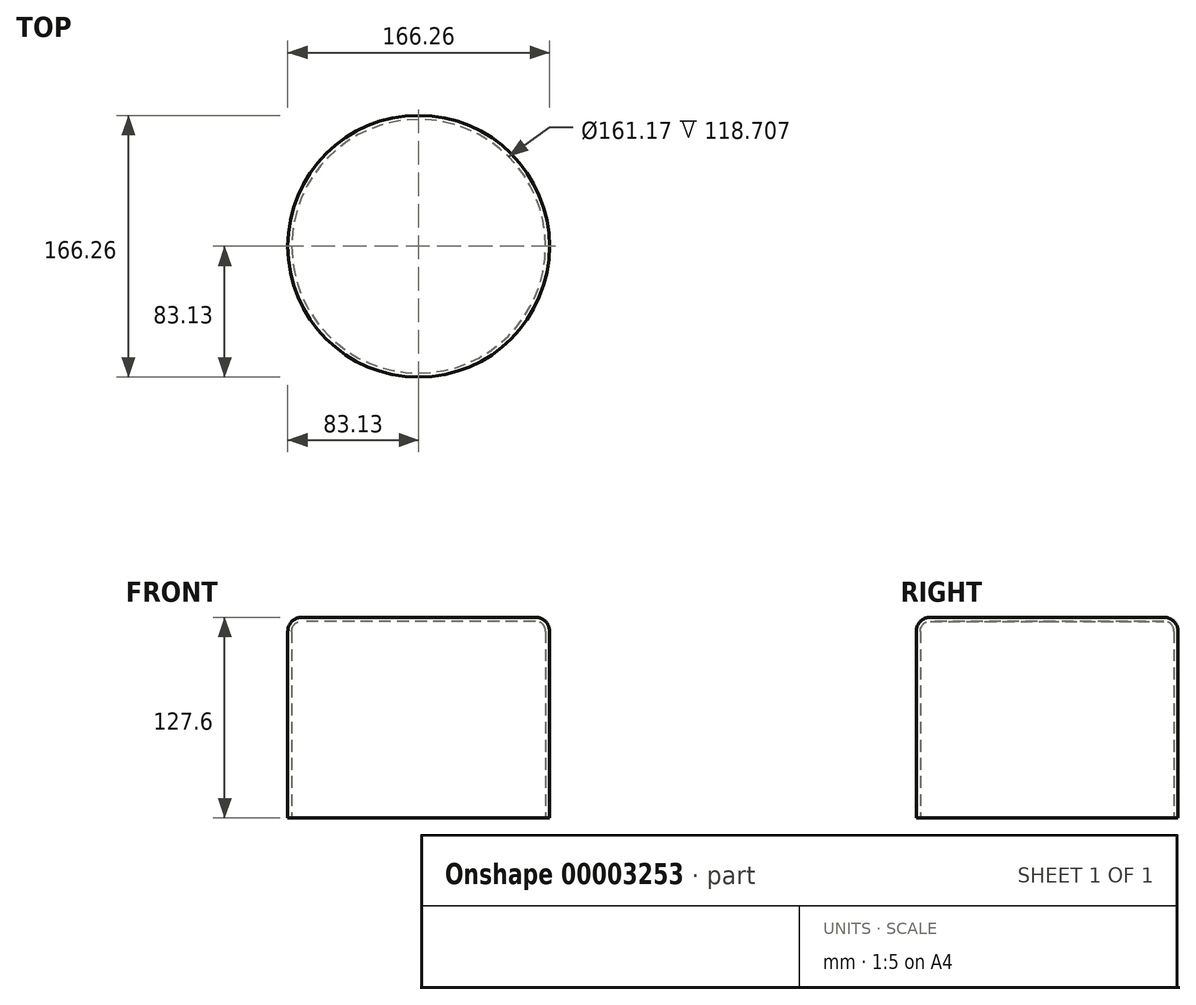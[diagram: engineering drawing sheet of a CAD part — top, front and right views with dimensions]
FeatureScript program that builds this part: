
annotation { "Feature Type Name" : "Feature", "Feature Type Description" : "" }
export const myFeature = defineFeature(function(context is Context, id is Id, definition is map)
    precondition{}
    {
        {
            var Q0;
            Q0=qCreatedBy(makeId("Top.planeOp"),FACE);
            var sketch = newSketch(context, id + "F0", { "sketchPlane" : qUnion([Q0])});
            skCircle(sketch, "E0", {"center": v(0, 0) * mm, "radius": 83.13 * mm});
            skSolve(sketch);
        }
        {
            var Q0;
            Q0=makeQuery(id+"F0.imprint","IMPRINT",FACE,{"disambiguationData":[TD([[makeQuery(id+"F0.imprint","IMPRINT",EDGE,{"derivedFrom":sQuery(id+"F0.wireOp",EDGE,"E0")}),1.0]])]});
            extrude(context, id + "F1", {"entities" : qUnion([Q0]), "depth" : 127.6 * mm});
        }
        {
            var Q0;
            Q0=makeQuery(id+"F1.opExtrude","CAP_FACE",FACE,{"disambiguationData":[OSD([sQuery(id+"F0.wireOp",EDGE,"E0")])],"isStart":false});
            fillet(context, id + "F2", {"entities" : qUnion([Q0]), "radius" : 8.9 * mm, "tangentPropagation" : true, "allowEdgeOverflow" : false});
        }
        {
            var Q0;
            Q0=makeQuery(id+"F1.opExtrude","CAP_FACE",FACE,{"disambiguationData":[OSD([sQuery(id+"F0.wireOp",EDGE,"E0")])],"isStart":true});
            shell(context, id + "F3", {"entities" : qUnion([Q0]), "thickness" : 2.54 * mm});
        }
    });
